# Revit family: Sanitary_Urinals_Hansgrohe_62010XXX-CreekTide-Q-Urinal-600-300-with__0001
name_source: partatom
category: Plumbing Fixtures
units: mm (PartAtom-declared; Revit-internal decimal feet)

## family parameters
Always vertical = No
Cut with Voids When Loaded = No
OmniClass Number = 23.31.21.00
OmniClass Title = Urinals
Part Type = Normal
Room Calculation Point = No
Round Connector Dimension = Use Diameter
Shared = No
Work Plane-Based = Yes

## types (1)
- 450 White
    Connector Description = Water Outlet 32 mm
    Default Elevation = 1219 mm
    Description = CreekTide Q Urinal 600/300 with rear water supply and bottom outlet rimless, HygieneEffect
    Diameter = 32 mm
    Inlet Connector Description = Cold Water Inlet 12.7 mm
    Inlet Diameter = 13 mm
    Manufacturer = Hansgrohe
    Material 1 = Hansgrohe - Metal - Chrome
    Material 2 = Hansgrohe - Ceramic - 452 White
    Model = 62010XXX
    Product Guid = 00699746-1770-41bf-93c5-232c24aa3f2d
    Product Page URL = https://pro.hansgrohe.com
    Product data url = https://bimobject.com
    URL = https://www.hansgrohe.com
    Version = 1

## geometry (parser evidence)
native form markers: Sweep x3
no freeform markers — native parametric forms only
